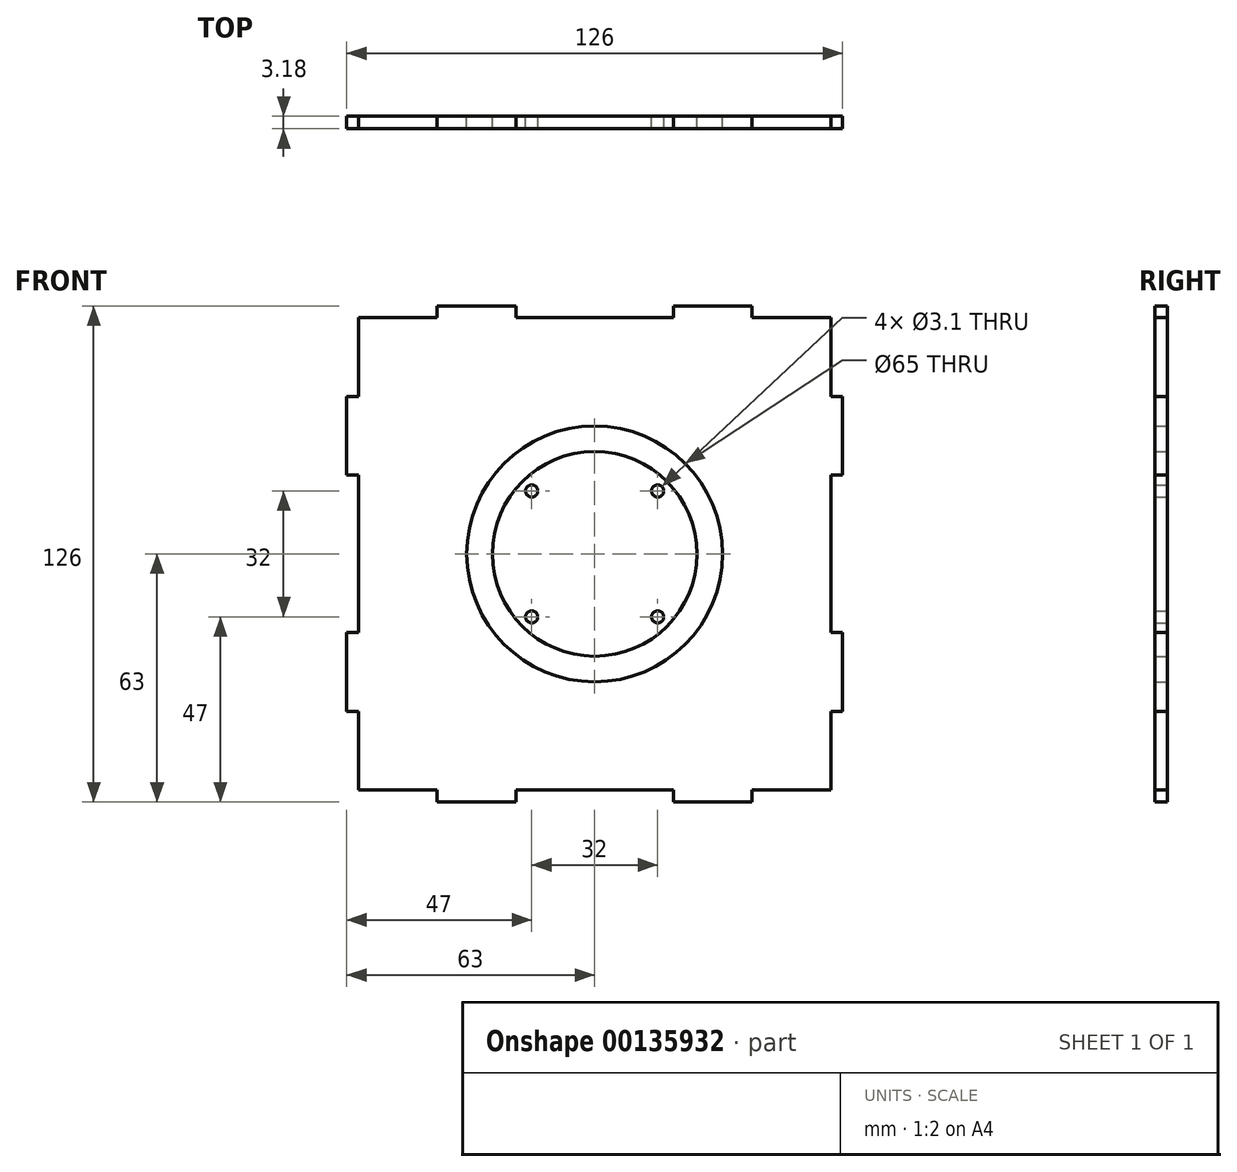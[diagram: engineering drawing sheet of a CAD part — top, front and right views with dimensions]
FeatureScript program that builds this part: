
annotation { "Feature Type Name" : "Feature", "Feature Type Description" : "" }
export const myFeature = defineFeature(function(context is Context, id is Id, definition is map)
    precondition{}
    {
        {
            var Q0;
            Q0=qCreatedBy(makeId("Front.planeOp"),FACE);
            var sketch = newSketch(context, id + "F0", { "sketchPlane" : qUnion([Q0])});
            skCircle(sketch, "E0", {"center": v(0, 0) * mm, "radius": 26 * mm});
            skCircle(sketch, "E1", {"center": v(0, 0) * mm, "radius": 32.5 * mm});
            skCircle(sketch, "E2", {"center": v(16, 16) * mm, "radius": 1.55 * mm});
            skCircle(sketch, "E3.1.0", {"center": v(-16, 16) * mm, "radius": 1.55 * mm});
            skCircle(sketch, "E3.2.0", {"center": v(-16, -16) * mm, "radius": 1.55 * mm});
            skCircle(sketch, "E3.3.0", {"center": v(16, -16) * mm, "radius": 1.55 * mm});
            skLineSegment(sketch, "E4", {"start": v(0, 60) * mm, "end": v(20, 60) * mm});
            skLineSegment(sketch, "E5", {"start": v(20, 60) * mm, "end": v(20, 63) * mm});
            skLineSegment(sketch, "E6", {"start": v(20, 63) * mm, "end": v(40, 63) * mm});
            skLineSegment(sketch, "E7", {"start": v(40, 63) * mm, "end": v(40, 60) * mm});
            skLineSegment(sketch, "E8", {"start": v(40, 60) * mm, "end": v(60, 60) * mm});
            skLineSegment(sketch, "E9", {"start": v(60, 60) * mm, "end": v(60, 40) * mm});
            skLineSegment(sketch, "E10", {"start": v(60, 40) * mm, "end": v(63, 40) * mm});
            skLineSegment(sketch, "E11", {"start": v(63, 40) * mm, "end": v(63, 20) * mm});
            skLineSegment(sketch, "E12", {"start": v(63, 20) * mm, "end": v(60, 20) * mm});
            skLineSegment(sketch, "E13", {"start": v(60, 20) * mm, "end": v(60, 0) * mm});
            skLineSegment(sketch, "E14.1.0", {"start": v(-60, 0) * mm, "end": v(-60, 20) * mm});
            skLineSegment(sketch, "E14.1.1", {"start": v(-63, 20) * mm, "end": v(-63, 40) * mm});
            skLineSegment(sketch, "E14.1.2", {"start": v(-60, 40) * mm, "end": v(-60, 60) * mm});
            skLineSegment(sketch, "E14.1.3", {"start": v(-60, 20) * mm, "end": v(-63, 20) * mm});
            skLineSegment(sketch, "E14.1.4", {"start": v(-63, 40) * mm, "end": v(-60, 40) * mm});
            skLineSegment(sketch, "E14.1.5", {"start": v(-60, 60) * mm, "end": v(-40, 60) * mm});
            skLineSegment(sketch, "E14.1.6", {"start": v(-40, 63) * mm, "end": v(-20, 63) * mm});
            skLineSegment(sketch, "E14.1.7", {"start": v(-20, 60) * mm, "end": v(0, 60) * mm});
            skLineSegment(sketch, "E14.1.8", {"start": v(-40, 60) * mm, "end": v(-40, 63) * mm});
            skLineSegment(sketch, "E14.1.9", {"start": v(-20, 63) * mm, "end": v(-20, 60) * mm});
            skLineSegment(sketch, "E14.2.0", {"start": v(0, -60) * mm, "end": v(-20, -60) * mm});
            skLineSegment(sketch, "E14.2.1", {"start": v(-20, -63) * mm, "end": v(-40, -63) * mm});
            skLineSegment(sketch, "E14.2.2", {"start": v(-40, -60) * mm, "end": v(-60, -60) * mm});
            skLineSegment(sketch, "E14.2.3", {"start": v(-20, -60) * mm, "end": v(-20, -63) * mm});
            skLineSegment(sketch, "E14.2.4", {"start": v(-40, -63) * mm, "end": v(-40, -60) * mm});
            skLineSegment(sketch, "E14.2.5", {"start": v(-60, -60) * mm, "end": v(-60, -40) * mm});
            skLineSegment(sketch, "E14.2.6", {"start": v(-63, -40) * mm, "end": v(-63, -20) * mm});
            skLineSegment(sketch, "E14.2.7", {"start": v(-60, -20) * mm, "end": v(-60, 0) * mm});
            skLineSegment(sketch, "E14.2.8", {"start": v(-60, -40) * mm, "end": v(-63, -40) * mm});
            skLineSegment(sketch, "E14.2.9", {"start": v(-63, -20) * mm, "end": v(-60, -20) * mm});
            skLineSegment(sketch, "E14.3.0", {"start": v(60, 0) * mm, "end": v(60, -20) * mm});
            skLineSegment(sketch, "E14.3.1", {"start": v(63, -20) * mm, "end": v(63, -40) * mm});
            skLineSegment(sketch, "E14.3.2", {"start": v(60, -40) * mm, "end": v(60, -60) * mm});
            skLineSegment(sketch, "E14.3.3", {"start": v(60, -20) * mm, "end": v(63, -20) * mm});
            skLineSegment(sketch, "E14.3.4", {"start": v(63, -40) * mm, "end": v(60, -40) * mm});
            skLineSegment(sketch, "E14.3.5", {"start": v(60, -60) * mm, "end": v(40, -60) * mm});
            skLineSegment(sketch, "E14.3.6", {"start": v(40, -63) * mm, "end": v(20, -63) * mm});
            skLineSegment(sketch, "E14.3.7", {"start": v(20, -60) * mm, "end": v(0, -60) * mm});
            skLineSegment(sketch, "E14.3.8", {"start": v(40, -60) * mm, "end": v(40, -63) * mm});
            skLineSegment(sketch, "E14.3.9", {"start": v(20, -63) * mm, "end": v(20, -60) * mm});
            skSolve(sketch);
        }
        {
            var Q0;
            Q0=makeQuery(id+"F0.imprint","IMPRINT",FACE,{"disambiguationData":[TD([[makeQuery(id+"F0.imprint","IMPRINT",EDGE,{"derivedFrom":sQuery(id+"F0.wireOp",EDGE,"E1")}),-1.0]])]});
            extrude(context, id + "F1", {"entities" : qUnion([Q0]), "depth" : 3.17 * mm, "symmetric" : true});
        }
        {
            var Q0;
            Q0=makeQuery(id+"F0.imprint","IMPRINT",FACE,{"disambiguationData":[TD([[makeQuery(id+"F0.imprint","IMPRINT",EDGE,{"derivedFrom":sQuery(id+"F0.wireOp",EDGE,"E0")}),1.0]])]});
            extrude(context, id + "F2", {"entities" : qUnion([Q0]), "depth" : 3.17 * mm, "symmetric" : true});
        }
    });
